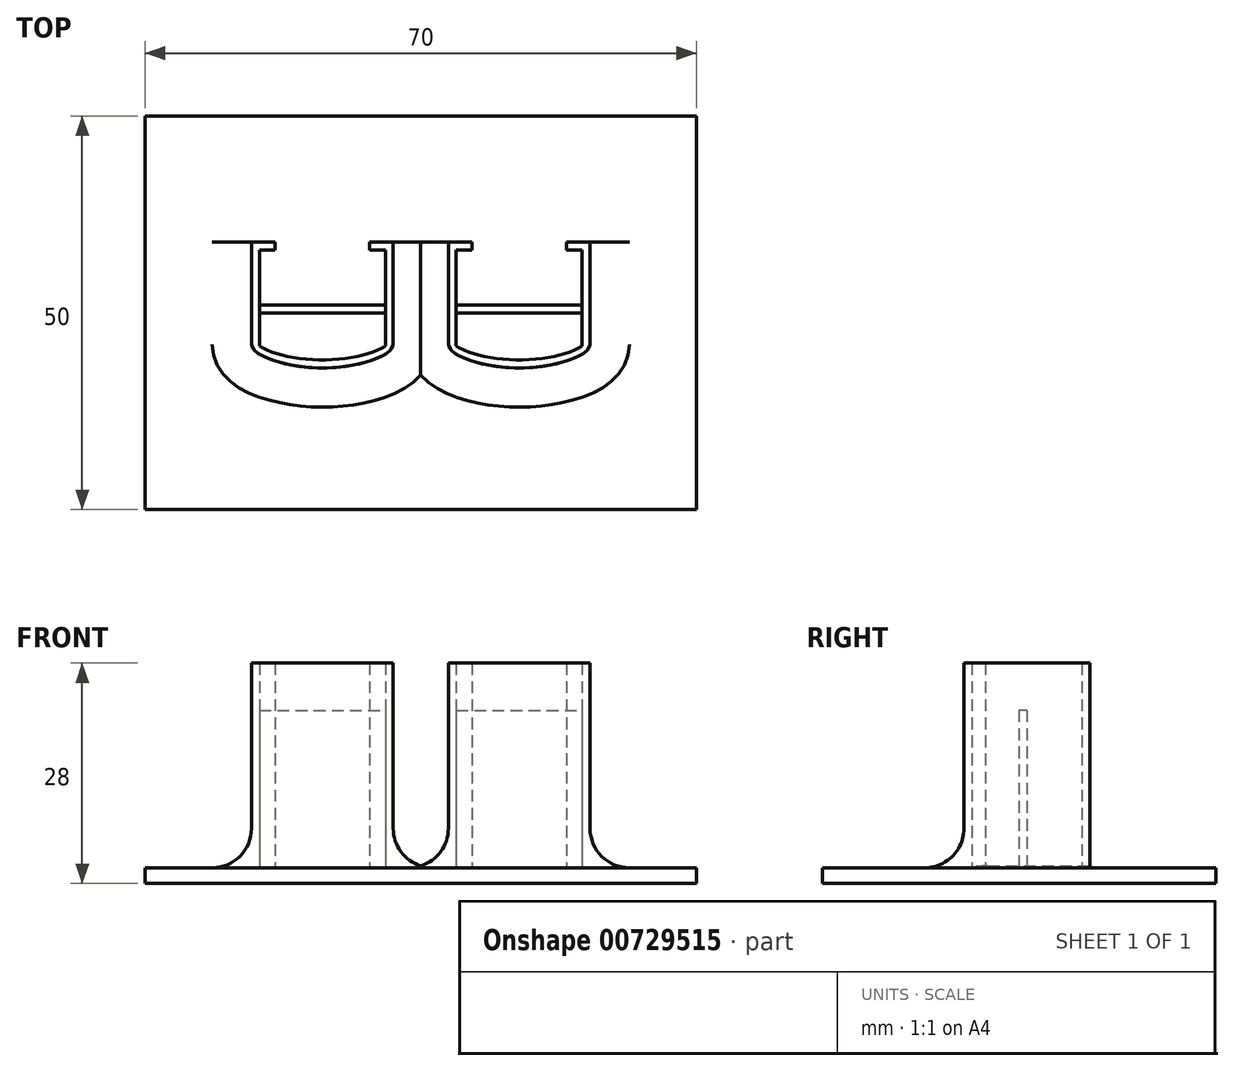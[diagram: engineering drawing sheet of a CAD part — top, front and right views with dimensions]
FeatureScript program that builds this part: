
annotation { "Feature Type Name" : "Feature", "Feature Type Description" : "" }
export const myFeature = defineFeature(function(context is Context, id is Id, definition is map)
    precondition{}
    {
        {
            var Q0;
            Q0=qCreatedBy(makeId("Top.planeOp"),FACE);
            var sketch = newSketch(context, id + "F0", { "sketchPlane" : qUnion([Q0])});
            skLineSegment(sketch, "E0", {"start": v(0, 0) * mm, "end": v(-9, 0) * mm, "construction": true});
            skLineSegment(sketch, "E1", {"start": v(0, 0) * mm, "end": v(9, 0) * mm, "construction": true});
            skLineSegment(sketch, "E2", {"start": v(0, 0) * mm, "end": v(0, 9) * mm, "construction": true});
            skLineSegment(sketch, "E3", {"start": v(0, 0) * mm, "end": v(0, -7) * mm, "construction": true});
            skLineSegment(sketch, "E4", {"start": v(-9, 0) * mm, "end": v(-9, 9) * mm});
            skLineSegment(sketch, "E5", {"start": v(9, 0) * mm, "end": v(9, 9) * mm});
            skLineSegment(sketch, "E6", {"start": v(-9, 9) * mm, "end": v(-6, 9) * mm});
            skLineSegment(sketch, "E7", {"start": v(9, 9) * mm, "end": v(6, 9) * mm});
            skLineSegment(sketch, "E8", {"start": v(-9, 0) * mm, "end": v(-9, -4) * mm});
            skLineSegment(sketch, "E9", {"start": v(9, 0) * mm, "end": v(9, -4) * mm});
            skLineSegment(sketch, "E10", {"start": v(0, 0) * mm, "end": v(0, -1) * mm, "construction": true});
            skFitSpline(sketch, "E11", {"points": [v(-9, -4) * mm, v(0, -7) * mm, v(9, -4) * mm, v(0, -1) * mm, v(-9, -4) * mm]});
            skLineSegment(sketch, "E12", {"start": v(0, 0) * mm, "end": v(0, 0) * mm});
            skLineSegment(sketch, "E13", {"start": v(0, 0) * mm, "end": v(0, -6) * mm, "construction": true});
            skLineSegment(sketch, "E14", {"start": v(-9, 0) * mm, "end": v(-9, -3) * mm, "construction": true});
            skLineSegment(sketch, "E15", {"start": v(9, 0) * mm, "end": v(9, -3) * mm, "construction": true});
            skFitSpline(sketch, "E16", {"points": [v(-9, -3) * mm, v(0, 0) * mm, v(9, -3) * mm, v(0, -6) * mm, v(-9, -3) * mm]});
            skLineSegment(sketch, "E17", {"start": v(-6, 9) * mm, "end": v(-6, 8) * mm});
            skLineSegment(sketch, "E18", {"start": v(6, 9) * mm, "end": v(6, 8) * mm});
            skLineSegment(sketch, "E19", {"start": v(6, 8) * mm, "end": v(8, 8) * mm});
            skLineSegment(sketch, "E20", {"start": v(-6, 8) * mm, "end": v(-8, 8) * mm});
            skLineSegment(sketch, "E21", {"start": v(-8, 8) * mm, "end": v(-8, -4.25) * mm});
            skLineSegment(sketch, "E22", {"start": v(8, 8) * mm, "end": v(8, -4.25) * mm});
            skPoint(sketch, "E23", {"position": v(-8, 0) * mm});
            skLineSegment(sketch, "E24.bottom", {"start": v(-8, 0) * mm, "end": v(8, 0) * mm});
            skLineSegment(sketch, "E24.top", {"start": v(-8, 1) * mm, "end": v(8, 1) * mm});
            skLineSegment(sketch, "E24.left", {"start": v(-8, 0) * mm, "end": v(-8, 1) * mm});
            skLineSegment(sketch, "E24.right", {"start": v(8, 0) * mm, "end": v(8, 1) * mm});
            skSolve(sketch);
        }
        {
            var Q0;
            {var subQ6=sQuery(id+"F0.wireOp",EDGE,"E4");Q0=makeQuery(id+"F0.imprint","IMPRINT",FACE,{"disambiguationData":[TD([[makeQuery(id+"F0.imprint","IMPRINT",EDGE,{"derivedFrom":subQ6}),-1.0]])]});}
            var Q1;
            {var subQ0=sQuery(id+"F0.wireOp",EDGE,"E21");var subQ1=sQuery(id+"F0.wireOp",EDGE,"E11");var subQ2=makeQuery(id+"F0.imprint","INTERSECT",VERTEX,{"derivedFrom":[subQ1,subQ0]});Q1=makeQuery(id+"F0.imprint","IMPRINT",FACE,{"disambiguationData":[TD([[makeQuery(id+"F0.imprint","IMPRINT",EDGE,{"disambiguationData":[TD([[subQ2,-1.0]])],"derivedFrom":subQ1}),-1.0]])]});}
            var Q2;
            {var subQ0=sQuery(id+"F0.wireOp",EDGE,"E11");var subQ1=sQuery(id+"F0.wireOp",EDGE,"E8");var subQ2=makeQuery(id+"F0.imprint","INTERSECT",VERTEX,{"derivedFrom":[subQ1,subQ0]});Q2=makeQuery(id+"F0.imprint","IMPRINT",FACE,{"disambiguationData":[TD([[makeQuery(id+"F0.imprint","IMPRINT",EDGE,{"disambiguationData":[TD([[subQ2,1.0]])],"derivedFrom":subQ1}),1.0]])]});}
            var Q3;
            {var subQ0=sQuery(id+"F0.wireOp",EDGE,"E21");var subQ1=sQuery(id+"F0.wireOp",EDGE,"E11");var subQ2=makeQuery(id+"F0.imprint","INTERSECT",VERTEX,{"derivedFrom":[subQ1,subQ0]});Q3=makeQuery(id+"F0.imprint","IMPRINT",FACE,{"disambiguationData":[TD([[makeQuery(id+"F0.imprint","IMPRINT",EDGE,{"disambiguationData":[TD([[subQ2,-1.0]])],"derivedFrom":subQ1}),1.0]])]});}
            var Q4;
            {var subQ0=sQuery(id+"F0.wireOp",EDGE,"E11");var subQ7=makeQuery(id+"F0.imprint","INTERSECT",VERTEX,{"derivedFrom":[sQuery(id+"F0.wireOp",EDGE,"E8"),subQ0]});Q4=makeQuery(id+"F0.imprint","IMPRINT",FACE,{"disambiguationData":[TD([[makeQuery(id+"F0.imprint","IMPRINT",EDGE,{"disambiguationData":[TD([[subQ7,-1.0]])],"derivedFrom":subQ0}),1.0]])]});}
            var Q5;
            {var subQ0=sQuery(id+"F0.wireOp",EDGE,"E16");var subQ1=sQuery(id+"F0.wireOp",EDGE,"E11");var subQ2=makeQuery(id+"F0.imprint","INTERSECT",VERTEX,{"disambiguationData":[OD(0.0)],"derivedFrom":[subQ1,subQ0]});Q5=makeQuery(id+"F0.imprint","IMPRINT",FACE,{"disambiguationData":[TD([[makeQuery(id+"F0.imprint","IMPRINT",EDGE,{"disambiguationData":[TD([[subQ2,-1.0]])],"derivedFrom":subQ1}),1.0]])]});}
            var Q6;
            {var subQ0=sQuery(id+"F0.wireOp",EDGE,"E16");var subQ1=sQuery(id+"F0.wireOp",EDGE,"E11");var subQ2=makeQuery(id+"F0.imprint","INTERSECT",VERTEX,{"disambiguationData":[OD(0.0)],"derivedFrom":[subQ1,subQ0]});Q6=makeQuery(id+"F0.imprint","IMPRINT",FACE,{"disambiguationData":[TD([[makeQuery(id+"F0.imprint","IMPRINT",EDGE,{"disambiguationData":[TD([[subQ2,-1.0]])],"derivedFrom":subQ1}),-1.0]])]});}
            var Q7;
            {var subQ5=sQuery(id+"F0.wireOp",EDGE,"E5");Q7=makeQuery(id+"F0.imprint","IMPRINT",FACE,{"disambiguationData":[TD([[makeQuery(id+"F0.imprint","IMPRINT",EDGE,{"derivedFrom":subQ5}),1.0]])]});}
            var Q8;
            {var subQ0=sQuery(id+"F0.wireOp",EDGE,"E11");var subQ1=sQuery(id+"F0.wireOp",EDGE,"E9");var subQ2=makeQuery(id+"F0.imprint","INTERSECT",VERTEX,{"derivedFrom":[subQ1,subQ0]});Q8=makeQuery(id+"F0.imprint","IMPRINT",FACE,{"disambiguationData":[TD([[makeQuery(id+"F0.imprint","IMPRINT",EDGE,{"disambiguationData":[TD([[subQ2,1.0]])],"derivedFrom":subQ1}),-1.0]])]});}
            extrude(context, id + "F1", {"entities" : qUnion([Q0, Q1, Q2, Q3, Q4, Q5, Q6, Q7, Q8]), "depth" : 26 * mm, "offsetDistance" : 25 * mm});
        }
        {
            var Q0;
            Q0=makeQuery(id+"F0.imprint","IMPRINT",FACE,{"disambiguationData":[TD([[makeQuery(id+"F0.imprint","IMPRINT",EDGE,{"derivedFrom":sQuery(id+"F0.wireOp",EDGE,"E24.top")}),-1.0]])]});
            extrude(context, id + "F2", {"entities" : qUnion([Q0]), "operationType" : NewBodyOperationType.ADD, "depth" : 20 * mm, "offsetDistance" : 25 * mm});
        }
        {
            var Q0;
            Q0=qCreatedBy(makeId("Top.planeOp"),FACE);
            var sketch = newSketch(context, id + "F3", { "sketchPlane" : qUnion([Q0])});
            skLineSegment(sketch, "E25", {"start": v(25, 0) * mm, "end": v(16, 0) * mm, "construction": true});
            skLineSegment(sketch, "E26", {"start": v(25, 0) * mm, "end": v(34, 0) * mm, "construction": true});
            skLineSegment(sketch, "E27", {"start": v(25, 0) * mm, "end": v(25, 9) * mm, "construction": true});
            skLineSegment(sketch, "E28", {"start": v(25, 0) * mm, "end": v(25, -7) * mm, "construction": true});
            skLineSegment(sketch, "E29", {"start": v(16, 0) * mm, "end": v(16, 9) * mm});
            skLineSegment(sketch, "E30", {"start": v(34, 0) * mm, "end": v(34, 9) * mm});
            skLineSegment(sketch, "E31", {"start": v(16, 9) * mm, "end": v(19, 9) * mm});
            skLineSegment(sketch, "E32", {"start": v(34, 9) * mm, "end": v(31, 9) * mm});
            skLineSegment(sketch, "E33", {"start": v(16, 0) * mm, "end": v(16, -4) * mm});
            skLineSegment(sketch, "E34", {"start": v(34, 0) * mm, "end": v(34, -4) * mm});
            skLineSegment(sketch, "E35", {"start": v(25, 0) * mm, "end": v(25, -1) * mm, "construction": true});
            skFitSpline(sketch, "E36", {"points": [v(16, -4) * mm, v(25, -7) * mm, v(34, -4) * mm, v(25, -1) * mm, v(16, -4) * mm]});
            skLineSegment(sketch, "E37", {"start": v(0, 0) * mm, "end": v(0, 0) * mm});
            skLineSegment(sketch, "E38", {"start": v(25, 0) * mm, "end": v(25, -6) * mm, "construction": true});
            skLineSegment(sketch, "E39", {"start": v(16, 0) * mm, "end": v(16, -3) * mm, "construction": true});
            skLineSegment(sketch, "E40", {"start": v(34, 0) * mm, "end": v(34, -3) * mm, "construction": true});
            skFitSpline(sketch, "E41", {"points": [v(16, -3) * mm, v(25, 0) * mm, v(34, -3) * mm, v(25, -6) * mm, v(16, -3) * mm]});
            skLineSegment(sketch, "E42", {"start": v(19, 9) * mm, "end": v(19, 8) * mm});
            skLineSegment(sketch, "E43", {"start": v(31, 9) * mm, "end": v(31, 8) * mm});
            skLineSegment(sketch, "E44", {"start": v(31, 8) * mm, "end": v(33, 8) * mm});
            skLineSegment(sketch, "E45", {"start": v(19, 8) * mm, "end": v(17, 8) * mm});
            skLineSegment(sketch, "E46", {"start": v(17, 8) * mm, "end": v(17, -4.25) * mm});
            skLineSegment(sketch, "E47", {"start": v(33, 8) * mm, "end": v(33, -4.25) * mm});
            skPoint(sketch, "E48", {"position": v(17, 0) * mm});
            skLineSegment(sketch, "E49.bottom", {"start": v(17, 0) * mm, "end": v(33, 0) * mm});
            skLineSegment(sketch, "E49.top", {"start": v(17, 1) * mm, "end": v(33, 1) * mm});
            skLineSegment(sketch, "E49.left", {"start": v(17, 0) * mm, "end": v(17, 1) * mm});
            skLineSegment(sketch, "E49.right", {"start": v(33, 0) * mm, "end": v(33, 1) * mm});
            skPoint(sketch, "E50", {"position": v(25, 9) * mm});
            skSolve(sketch);
        }
        {
            var Q0;
            {var subQ5=sQuery(id+"F3.wireOp",EDGE,"E29");Q0=makeQuery(id+"F3.imprint","IMPRINT",FACE,{"disambiguationData":[TD([[makeQuery(id+"F3.imprint","IMPRINT",EDGE,{"derivedFrom":subQ5}),-1.0]])]});}
            var Q1;
            {var subQ5=sQuery(id+"F3.wireOp",EDGE,"E30");Q1=makeQuery(id+"F3.imprint","IMPRINT",FACE,{"disambiguationData":[TD([[makeQuery(id+"F3.imprint","IMPRINT",EDGE,{"derivedFrom":subQ5}),1.0]])]});}
            var Q2;
            {var subQ2=sQuery(id+"F3.wireOp",EDGE,"E36");var subQ4=makeQuery(id+"F3.imprint","INTERSECT",VERTEX,{"derivedFrom":[sQuery(id+"F3.wireOp",EDGE,"E33"),subQ2]});Q2=makeQuery(id+"F3.imprint","IMPRINT",FACE,{"disambiguationData":[TD([[makeQuery(id+"F3.imprint","IMPRINT",EDGE,{"disambiguationData":[TD([[subQ4,-1.0]])],"derivedFrom":subQ2}),1.0]])]});}
            var Q3;
            {var subQ0=sQuery(id+"F3.wireOp",EDGE,"E41");var subQ1=sQuery(id+"F3.wireOp",EDGE,"E36");var subQ2=makeQuery(id+"F3.imprint","INTERSECT",VERTEX,{"disambiguationData":[OD(0.0)],"derivedFrom":[subQ1,subQ0]});Q3=makeQuery(id+"F3.imprint","IMPRINT",FACE,{"disambiguationData":[TD([[makeQuery(id+"F3.imprint","IMPRINT",EDGE,{"disambiguationData":[TD([[subQ2,-1.0]])],"derivedFrom":subQ1}),1.0]])]});}
            var Q4;
            {var subQ0=sQuery(id+"F3.wireOp",EDGE,"E41");var subQ1=sQuery(id+"F3.wireOp",EDGE,"E36");var subQ2=makeQuery(id+"F3.imprint","INTERSECT",VERTEX,{"disambiguationData":[OD(0.0)],"derivedFrom":[subQ1,subQ0]});Q4=makeQuery(id+"F3.imprint","IMPRINT",FACE,{"disambiguationData":[TD([[makeQuery(id+"F3.imprint","IMPRINT",EDGE,{"disambiguationData":[TD([[subQ2,-1.0]])],"derivedFrom":subQ1}),-1.0]])]});}
            var Q5;
            {var subQ0=sQuery(id+"F3.wireOp",EDGE,"E36");var subQ1=sQuery(id+"F3.wireOp",EDGE,"E33");var subQ2=makeQuery(id+"F3.imprint","INTERSECT",VERTEX,{"derivedFrom":[subQ1,subQ0]});Q5=makeQuery(id+"F3.imprint","IMPRINT",FACE,{"disambiguationData":[TD([[makeQuery(id+"F3.imprint","IMPRINT",EDGE,{"disambiguationData":[TD([[subQ2,1.0]])],"derivedFrom":subQ1}),1.0]])]});}
            var Q6;
            {var subQ0=sQuery(id+"F3.wireOp",EDGE,"E46");var subQ1=sQuery(id+"F3.wireOp",EDGE,"E36");var subQ2=makeQuery(id+"F3.imprint","INTERSECT",VERTEX,{"derivedFrom":[subQ1,subQ0]});Q6=makeQuery(id+"F3.imprint","IMPRINT",FACE,{"disambiguationData":[TD([[makeQuery(id+"F3.imprint","IMPRINT",EDGE,{"disambiguationData":[TD([[subQ2,-1.0]])],"derivedFrom":subQ1}),-1.0]])]});}
            var Q7;
            {var subQ0=sQuery(id+"F3.wireOp",EDGE,"E46");var subQ1=sQuery(id+"F3.wireOp",EDGE,"E36");var subQ2=makeQuery(id+"F3.imprint","INTERSECT",VERTEX,{"derivedFrom":[subQ1,subQ0]});Q7=makeQuery(id+"F3.imprint","IMPRINT",FACE,{"disambiguationData":[TD([[makeQuery(id+"F3.imprint","IMPRINT",EDGE,{"disambiguationData":[TD([[subQ2,-1.0]])],"derivedFrom":subQ1}),1.0]])]});}
            var Q8;
            {var subQ0=sQuery(id+"F3.wireOp",EDGE,"E36");var subQ1=sQuery(id+"F3.wireOp",EDGE,"E34");var subQ2=makeQuery(id+"F3.imprint","INTERSECT",VERTEX,{"derivedFrom":[subQ1,subQ0]});Q8=makeQuery(id+"F3.imprint","IMPRINT",FACE,{"disambiguationData":[TD([[makeQuery(id+"F3.imprint","IMPRINT",EDGE,{"disambiguationData":[TD([[subQ2,1.0]])],"derivedFrom":subQ1}),-1.0]])]});}
            extrude(context, id + "F4", {"entities" : qUnion([Q0, Q1, Q2, Q3, Q4, Q5, Q6, Q7, Q8]), "operationType" : NewBodyOperationType.ADD, "depth" : 26 * mm, "offsetDistance" : 25 * mm});
        }
        {
            var Q0;
            Q0=makeQuery(id+"F3.imprint","IMPRINT",FACE,{"disambiguationData":[TD([[makeQuery(id+"F3.imprint","IMPRINT",EDGE,{"derivedFrom":sQuery(id+"F3.wireOp",EDGE,"E49.top")}),-1.0]])]});
            extrude(context, id + "F5", {"entities" : qUnion([Q0]), "operationType" : NewBodyOperationType.ADD, "depth" : 20 * mm, "offsetDistance" : 25 * mm});
        }
        {
            var Q0;
            Q0=qCreatedBy(makeId("Top.planeOp"),FACE);
            var sketch = newSketch(context, id + "F6", { "sketchPlane" : qUnion([Q0])});
            skLineSegment(sketch, "E51.bottom", {"start": v(-22.5, 25) * mm, "end": v(47.5, 25) * mm});
            skLineSegment(sketch, "E51.top", {"start": v(-22.5, -25) * mm, "end": v(47.5, -25) * mm});
            skLineSegment(sketch, "E51.left", {"start": v(-22.5, 25) * mm, "end": v(-22.5, -25) * mm});
            skLineSegment(sketch, "E51.right", {"start": v(47.5, 25) * mm, "end": v(47.5, -25) * mm});
            skPoint(sketch, "E52", {"position": v(12.5, 25) * mm});
            skPoint(sketch, "E53", {"position": v(47.5, 0) * mm});
            skSolve(sketch);
        }
        {
            var Q0;
            Q0 = qSketchRegion(id + "F6", true);
            extrude(context, id + "F7", {"entities" : qUnion([Q0]), "operationType" : NewBodyOperationType.ADD, "oppositeDirection" : true, "depth" : 2 * mm, "offsetDistance" : 25 * mm});
        }
        {
            var Q0;
            Q0=makeQuery(id+"F1.opExtrude","CAP_EDGE",EDGE,{"disambiguationData":[OSD([sQuery(id+"F0.wireOp",EDGE,"E11")])],"isStart":true});
            fillet(context, id + "F8", {"entities" : qUnion([Q0]), "radius" : 5 * mm, "tangentPropagation" : true, "allowEdgeOverflow" : false});
        }
        {
            var Q0;
            Q0=makeQuery(id+"F4.opExtrude","CAP_EDGE",EDGE,{"disambiguationData":[OSD([sQuery(id+"F3.wireOp",EDGE,"E36")])],"isStart":true});
            fillet(context, id + "F9", {"entities" : qUnion([Q0]), "radius" : 5 * mm, "tangentPropagation" : true, "allowEdgeOverflow" : false});
        }
    });
